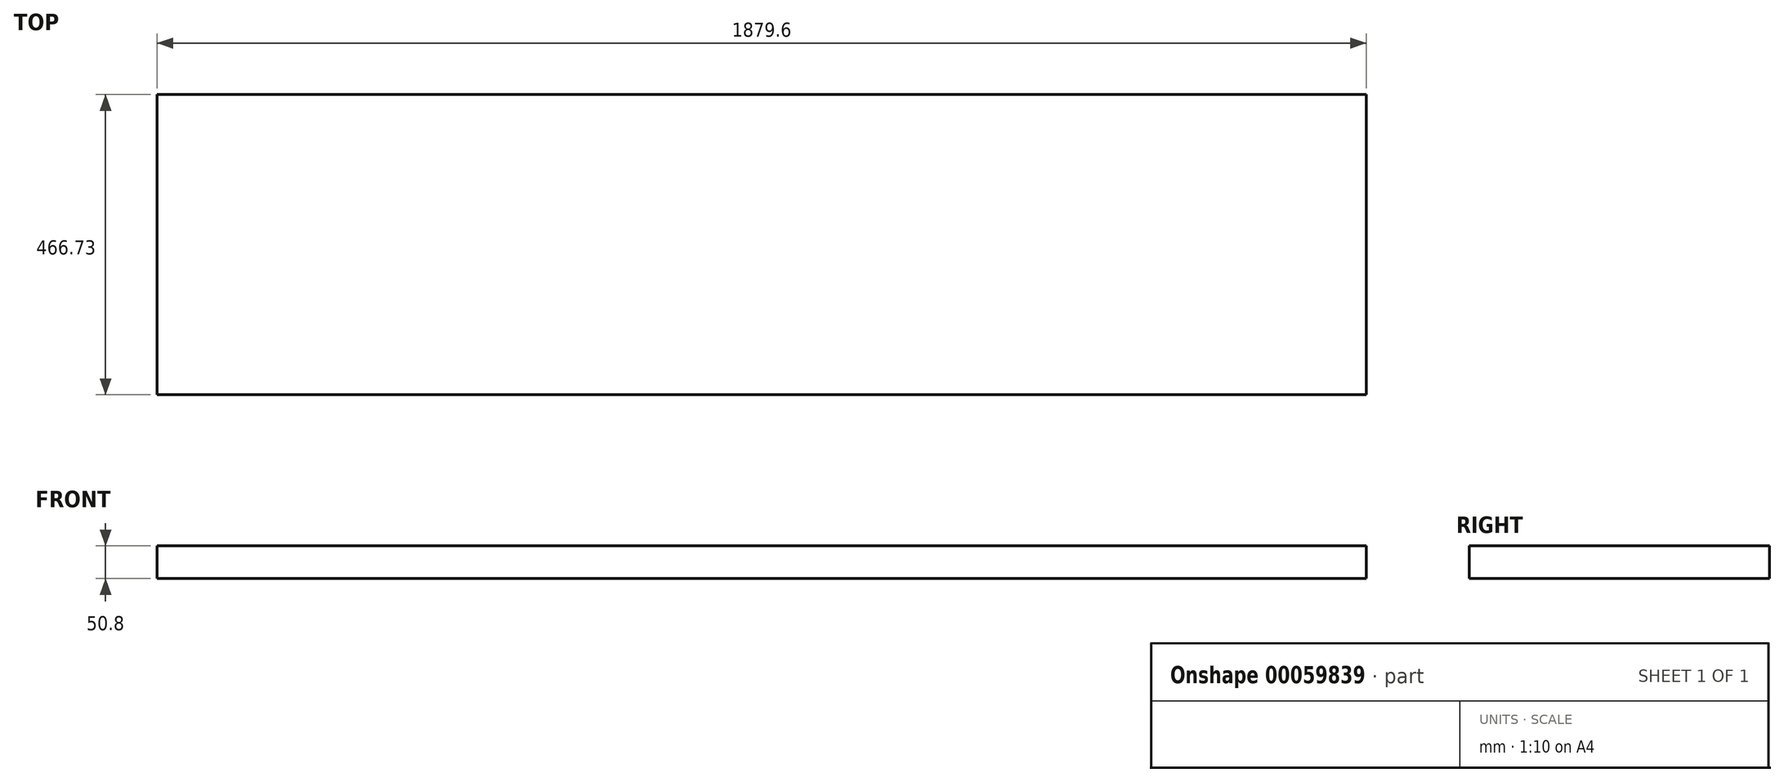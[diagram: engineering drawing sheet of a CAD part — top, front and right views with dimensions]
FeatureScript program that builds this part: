
annotation { "Feature Type Name" : "Feature", "Feature Type Description" : "" }
export const myFeature = defineFeature(function(context is Context, id is Id, definition is map)
    precondition{}
    {
        {
            var Q0;
            Q0=qCreatedBy(makeId("Front.planeOp"),FACE);
            var sketch = newSketch(context, id + "F0", { "sketchPlane" : qUnion([Q0])});
            skLineSegment(sketch, "E0.bottom", {"start": v(-969.51, -57.3) * mm, "end": v(910.09, -57.3) * mm});
            skLineSegment(sketch, "E0.top", {"start": v(-969.51, -6.5) * mm, "end": v(910.09, -6.5) * mm});
            skLineSegment(sketch, "E0.left", {"start": v(-969.51, -57.3) * mm, "end": v(-969.51, -6.5) * mm});
            skLineSegment(sketch, "E0.right", {"start": v(910.09, -57.3) * mm, "end": v(910.09, -6.5) * mm});
            skSolve(sketch);
        }
        {
            var Q0;
            Q0 = qSketchRegion(id + "F0", true);
            extrude(context, id + "F1", {"entities" : qUnion([Q0]), "depth" : 466.72 * mm});
        }
    });
